# Revit family: 00-9036-CV-A1
name_source: partatom
category: Luminarias
units: mm (PartAtom-declared; Revit-internal decimal feet)

## family parameters
Anfitrión = Cara
Compartido = Sí
Corte con vacíos al cargar = No
Cota de conector redondo = Diámetro de uso
Número OmniClass = 23.80.70.00
Origen de luz = No
Punto de cálculo de habitación = No
Tipo de pieza = Normal
Título OmniClass = Lighting

## types (1)
- 00-9036-CV-A1
    Acabado = Multi-coloured
    CRI = 0
    Carga aparente = 0 VA
    Catálogo = Decorative
    CodigoGubimclass = 50.60.50.20
    CodigoOmniclass = 21-04 50 40
    CodigoUniclass2015 = EF_70_80
    CodigoUniformat2010 = D5040
    DescripcionGubimclass = Iluminación interior
    DescripcionOmniclass = Lighting
    DescripcionUniclass2015 = Lighting
    DescripcionUniformat2010 = Lighting
    EAN13 = 8445386732077
    Eficiencia energética = NA EPREL
    Elevación por defecto = 1000 mm  [stored 3.28084 ft]
    Etiqueta V/f = 100-240V/50-60Hz
    Fabricante = LEDS C4
    Familia = Keops 2 Bodies Big
    FechaVersion = Creada: 09/03/2024
    Ficha = https://files.ledsc4.com
    Fotometría = https://files.ledsc4.com
    IMC = https://files.ledsc4.com
    IP = IP20
    IfcExportAs = IfcLightFixture
IfcLightFixture
    IfcExportType = NOTDEFINED
    Imagen web = https://files.ledsc4.com
    LDT = https://files.ledsc4.com
    Lumenes reales (lm) = 576
    Material = Aluminium
    Peso neto (KG) = 1.71
    Producto descatalogado = Catalogado EN
    Rayo de luz = SPOT+HONEYCOMB
    Referencia = 00-9036-CV-A1
    Tender text (Castellano) = LedsC4 Keops 2 Bodies Big 00-9036-CV-A1  Pendant for indoor use.  Structure material: Aluminium. Structure finish: Multi-coloured. Warranty: 5 Years.  Product net weight (Kg): 1.71 Product width or diameter (mm): 500 Product height (mm): 2800  Class 2. IP: IP20. Total power: 15. Power factor: NULL.
    Tender text (English) = LedsC4 Keops 2 Bodies Big 00-9036-CV-A1  Pendant for indoor use.  Structure material: Aluminium. Structure finish: Multi-coloured. Warranty: 5 Years.  Product net weight (Kg): 1.71 Product width or diameter (mm): 500 Product height (mm): 2800  Class 2. IP: IP20. Total power: 15. Power factor: NULL.
    Tipo = Pendant
    Vatios (W) = 15
    Versión = v1

note: [stored X ft] marks values corroborated as IEEE doubles in the binary element streams (Revit-internal decimal feet)
